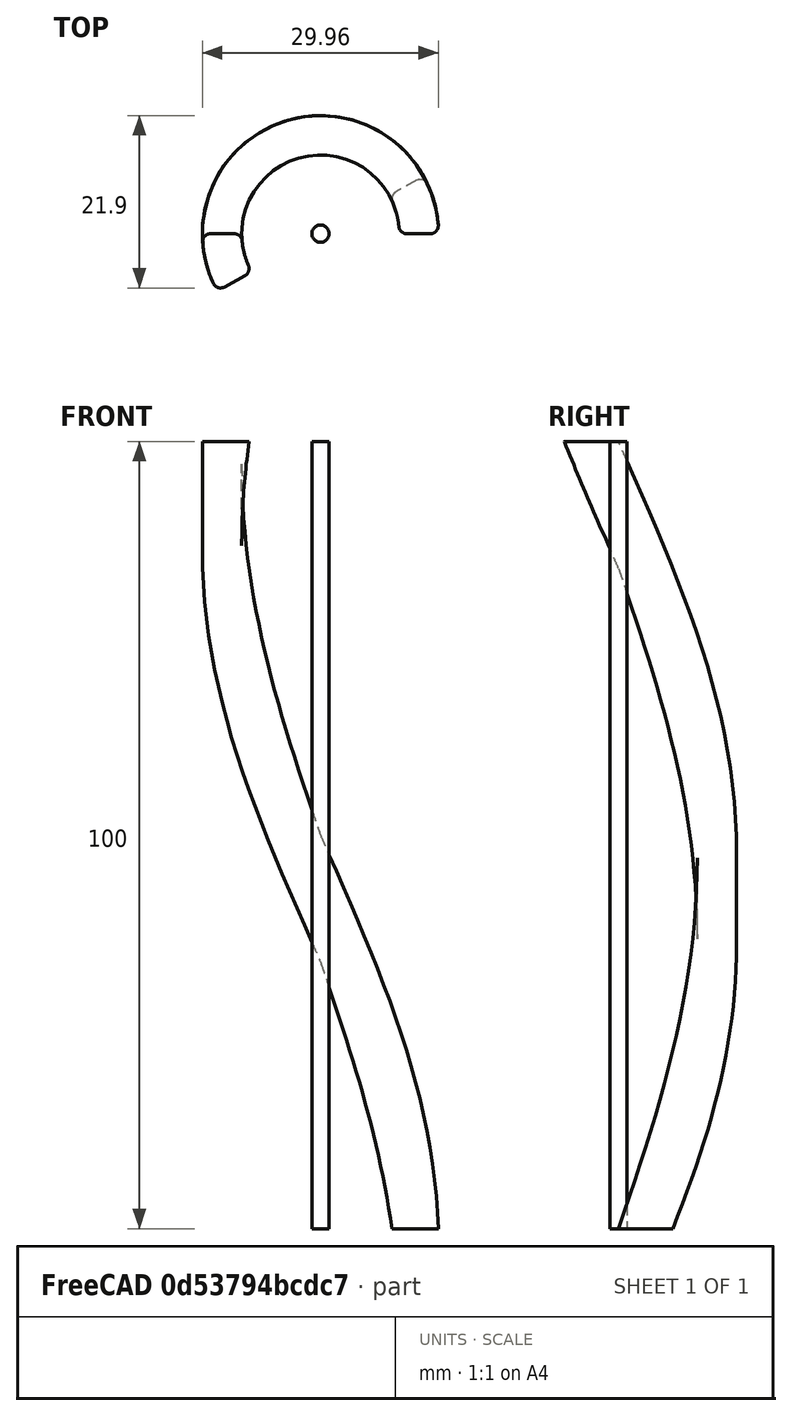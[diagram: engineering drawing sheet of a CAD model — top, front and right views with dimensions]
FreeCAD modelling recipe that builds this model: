
FCSTD DOCUMENT  (FreeCAD 0.20R25310 +2 (Git))
Label: Lahnkabel
License: All rights reserved
LicenseURL: http://en.wikipedia.org/wiki/All_rights_reserved
objects: Sketcher::SketchObject×2, PartDesign::Body×2, Part::FeaturePython×2, Raytracing::RayFeature×2, PartDesign::AdditiveHelix×1, PartDesign::Pad×1, Raytracing::RayProject×1
note: 8 computed .brp shape members not serialized (recipe doc carries the construction recipe); baked Part::Feature solids carry a one-line shape summary decoded from their .brp

FEATURE [Sketcher::SketchObject] Sketch001
  FullyConstrained = true
  MapMode = 5
  Support = -> [XY_Plane001]
  sketch-geometry (8):
    g0: ArcOfCircle CenterX=0 CenterY=0 CenterZ=0 NormalX=0 NormalY=0 NormalZ=1 AngleXU=0 Radius=15 StartAngle=0.0714894 EndAngle=0.434656
    g1: ArcOfCircle CenterX=0 CenterY=0 CenterZ=0 NormalX=0 NormalY=0 NormalZ=1 AngleXU=0 Radius=10 StartAngle=0.0910348 EndAngle=0.415111
    g2: LineSegment StartX=9.58098 StartY=5.31082 StartZ=0 EndX=12.2134 EndY=6.77 EndZ=0
    g3: LineSegment StartX=10.9545 StartY=0 StartZ=0 EndX=13.9642 EndY=0 EndZ=0
    g4: ArcOfCircle CenterX=10.0658 CenterY=4.4362 CenterZ=0 NormalX=0 NormalY=0 NormalZ=1 AngleXU=0 Radius=1 StartAngle=2.07694 EndAngle=3.5567
    g5: ArcOfCircle CenterX=12.6982 CenterY=5.89538 CenterZ=0 NormalX=0 NormalY=0 NormalZ=1 AngleXU=0 Radius=1 StartAngle=0.434656 EndAngle=2.07694
    g6: ArcOfCircle CenterX=10.9545 CenterY=1 CenterZ=0 NormalX=0 NormalY=0 NormalZ=1 AngleXU=0 Radius=1 StartAngle=3.23263 EndAngle=4.71239
    g7: ArcOfCircle CenterX=13.9642 CenterY=1 CenterZ=0 NormalX=0 NormalY=0 NormalZ=1 AngleXU=0 Radius=1 StartAngle=4.71239 EndAngle=6.35467
  constraints (20):
    c: Coincident(g0,g-1)
    c: Coincident(g1,g0)
    c: PointOnObject(g0,g3)
    c: Equal(g4,g5)
    c: Equal(g4,g6)
    c: Equal(g4,g7)
    c: Radius(g4) = 1
    c: Tangent(g4,g1) = 1.5708
    c: Tangent(g4,g2) = 1.5708
    c: Tangent(g5,g2) = 1.5708
    c: Tangent(g5,g0) = -1.5708
    c: Tangent(g7,g0) = -1.5708
    c: Tangent(g7,g3) = -1.5708
    c: Tangent(g6,g3) = -1.5708
    c: Tangent(g6,g1) = 1.5708
    c: PointOnObject(g3,g-1)
    c: Radius(g1) = 10
    c: Radius(g0) = 15
    c: PointOnObject(g0,g2)
    c: Angle(g3,g2) = 0.506145
FEATURE [PartDesign::AdditiveHelix] AdditiveHelix
  Angle = 0
  Axis = (-3e-16,3e-16,1)
  Base = (0,0,0)
  Growth = 0
  HasBeenEdited = true
  Height = 100
  LeftHanded = false
  Mode = 2
  Outside = false
  Pitch = 200
  Profile = -> Sketch001
  ReferenceAxis = -> Z_Axis001
  Refine = true
  Turns = 0.5
FEATURE [PartDesign::Body] Body001
  Group = -> [Sketch001,AdditiveHelix]
  Origin = -> Origin001
  Tip = -> AdditiveHelix
FEATURE [Part::FeaturePython] Array  # Draft array (typed FeaturePython)
  Angle = 360
  ArrayType = 1
  Axis = (0,0,1)
  Base = -> Body001
  Center = (0,0,0)
  Count = 12
  ExpandArray = false
  Fuse = false
  IntervalAxis = (0,0,0)
  IntervalX = (50,0,0)
  IntervalY = (0,50,0)
  IntervalZ = (0,0,50)
  NumberCircles = 3
  NumberPolar = 12
  NumberX = 2
  NumberY = 2
  NumberZ = 1
  PlacementList = 12 placements: [(0,0,0),(0,0,0),(0,0,0),(0,0,0),(0,0,0),(0,0,0),(0,0,0),(0,0,0),(0,0,0),(0,0,0),(0,0,0),(0,0,0)]
  RadialDistance = 50
  ScaleList = (12) [(1,1,1),(1,1,1),(1,1,1),(1,1,1),(1,1,1),(1,1,1),(1,1,1),(1,1,1),(1,1,1),(1,1,1),(1,1,1),(1,1,1)]
  Symmetry = 1
  TangentialDistance = 25
FEATURE [Raytracing::RayFeature] Array_View
  Result = <blob: 1308824 chars omitted>
  Source = -> Array
  Transparency = 0
FEATURE [Sketcher::SketchObject] Sketch002
  FullyConstrained = true
  MapMode = 5
  Support = -> [XY_Plane002]
  sketch-geometry (1):
    g0: Circle CenterX=0 CenterY=0 CenterZ=0 NormalX=0 NormalY=0 NormalZ=1 AngleXU=0 Radius=1.1
  constraints (2):
    c: Coincident(g0,g-1)
    c: Diameter(g0) = 2.2
FEATURE [PartDesign::Pad] Pad001
  Direction = (0,0,1)
  Length = 100
  Length2 = 100
  Profile = -> Sketch002
  Refine = true
  Type = 0
FEATURE [PartDesign::Body] Body002
  Group = -> [Sketch002,Pad001]
  Origin = -> Origin002
  Tip = -> Pad001
FEATURE [Part::FeaturePython] Array001  # Draft array (typed FeaturePython)
  Angle = 360
  ArrayType = 2
  Axis = (0,0,1)
  Base = -> Body002
  Center = (0,0,0)
  Count = 62
  ExpandArray = false
  Fuse = false
  IntervalAxis = (0,0,0)
  IntervalX = (50,0,0)
  IntervalY = (0,50,0)
  IntervalZ = (0,0,50)
  NumberCircles = 5
  NumberPolar = 5
  NumberX = 2
  NumberY = 2
  NumberZ = 1
  PlacementList = 62 placements: [(0,0,0),(-2.2,0,0),(-1.1,-1.90526,0),(1.1,-1.90526,0),(2.2,-2.69422e-16,0),(1.1,1.90526,0),(-1.1,1.90526,0),(-4.4,0,0),(-3.81051,-2.2,0),(-2.2,-3.81051,0),(-8.88178e-16,-4.4,0),(2.2,-3.81051,0),(3.81051,-2.2,0),(4.4,-5.38845e-16,0),(3.81051,2.2,0),(2.2,3.81051,0),(8.88178e-16,4.4,0),(-2.2,3.81051,0),(-3.81051,2.2,0),(-6.6,0,0),(-6.20197,-2.25733,0),(-5.05589,-4.2424,0),(-3.3,-5.71577,0),+39 more]
  RadialDistance = 2.2
  ScaleList = (62) [(1,1,1),(1,1,1),(1,1,1),(1,1,1),(1,1,1),(1,1,1),(1,1,1),(1,1,1),(1,1,1),(1,1,1),(1,1,1),(1,1,1),(1,1,1),(1,1,1),(1,1,1),(1,1,1),(1,1,1),(1,1,1),+44 more]
  Symmetry = 1
  TangentialDistance = 2.2
FEATURE [Raytracing::RayFeature] Array001_View
  Result = <blob: 459550 chars omitted>
  Source = -> Array001
  Transparency = 0
FEATURE [Raytracing::RayProject] PovProject
  Camera = // declares position and view direction\n\n// Generated by FreeCAD (http://www.freecadweb.org/)\n#declare cam_location =  <41.3533,155.822,-71.2024>;\n#declare cam_look_at  = <-11.3949,69.6075,22.8365>;\n#declare cam_sky      = <-0.390687,0.777155,0.493349>;\n#declare cam_angle    = 45; \ncamera {\n  location  cam_location\n  look_at   cam_look_at\n  sky       cam_sky\n  angle     cam_angle \n  right x*1200/900\n}
  Group = -> [Array_View,Array001_View]
  Template = <path>
note: 1 file-system path scrubbed to <path> (originals preserved in the JSON sidecar)
